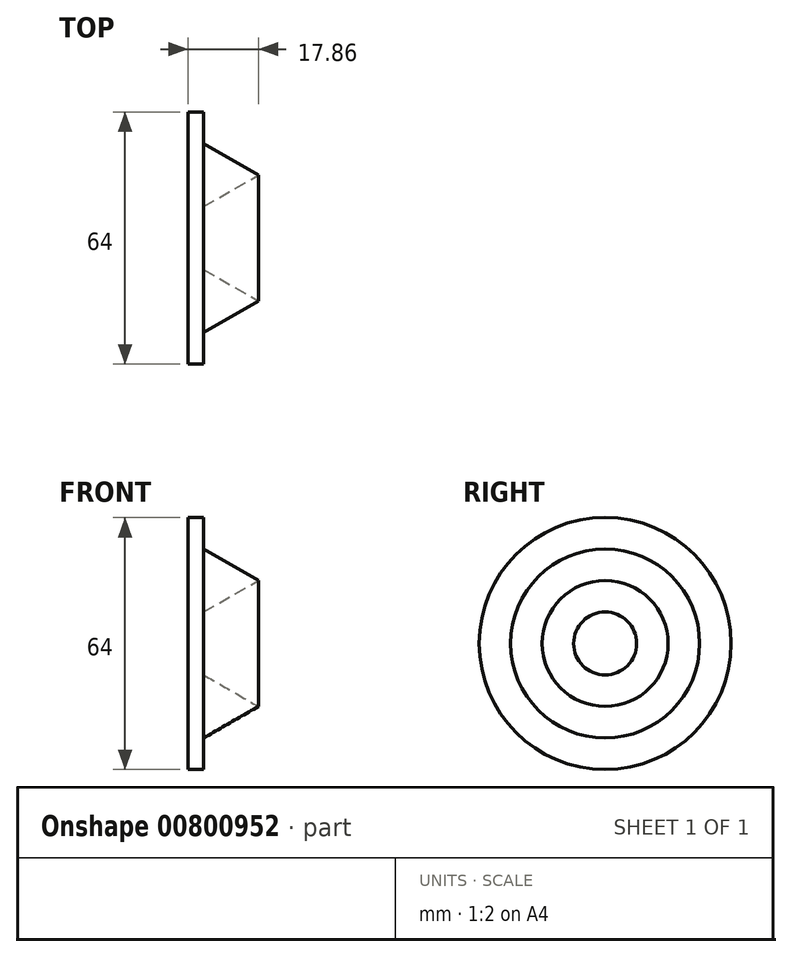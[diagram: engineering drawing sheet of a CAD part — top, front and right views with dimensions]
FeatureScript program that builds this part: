
annotation { "Feature Type Name" : "Feature", "Feature Type Description" : "" }
export const myFeature = defineFeature(function(context is Context, id is Id, definition is map)
    precondition{}
    {
        {
            var Q0;
            Q0=qCreatedBy(makeId("Top.planeOp"),FACE);
            var sketch = newSketch(context, id + "F0", { "sketchPlane" : qUnion([Q0])});
            skLineSegment(sketch, "E0", {"start": v(0, 0) * mm, "end": v(0, -32) * mm});
            skLineSegment(sketch, "E1", {"start": v(0, -32) * mm, "end": v(4, -32) * mm});
            skLineSegment(sketch, "E2", {"start": v(4, -32) * mm, "end": v(4, -24) * mm});
            skLineSegment(sketch, "E3", {"start": v(4, -24) * mm, "end": v(17.86, -16) * mm});
            skLineSegment(sketch, "E4", {"start": v(17.86, -16) * mm, "end": v(4, -8) * mm});
            skLineSegment(sketch, "E5", {"start": v(4, -8) * mm, "end": v(4, 0) * mm});
            skLineSegment(sketch, "E6", {"start": v(4, 0) * mm, "end": v(0, 0) * mm});
            skLineSegment(sketch, "E7", {"start": v(4, -12.62) * mm, "end": v(4, -19.38) * mm});
            skLineSegment(sketch, "E8", {"start": v(4, -19.38) * mm, "end": v(9.86, -16) * mm});
            skLineSegment(sketch, "E9", {"start": v(9.86, -16) * mm, "end": v(4, -12.62) * mm});
            skSolve(sketch);
        }
        {
            var Q0;
            Q0=makeQuery(id+"F0.imprint","IMPRINT",FACE,{"disambiguationData":[TD([[makeQuery(id+"F0.imprint","IMPRINT",EDGE,{"derivedFrom":sQuery(id+"F0.wireOp",EDGE,"E0")}),1.0]])]});
            var Q1;
            Q1=makeQuery(id+"F0.imprint","IMPRINT",FACE,{"disambiguationData":[TD([[makeQuery(id+"F0.imprint","IMPRINT",EDGE,{"derivedFrom":sQuery(id+"F0.wireOp",EDGE,"E7")}),1.0]])]});
            var Q2;
            Q2=sQuery(id+"F0.wireOp",EDGE,"E6");
            revolve(context, id + "F1", {"surfaceOperationType" : NewSurfaceOperationType.NEW, "entities" : qUnion([Q0, Q1]), "axis" : qUnion([Q2]), "revolveType" : RevolveType.FULL});
        }
    });
